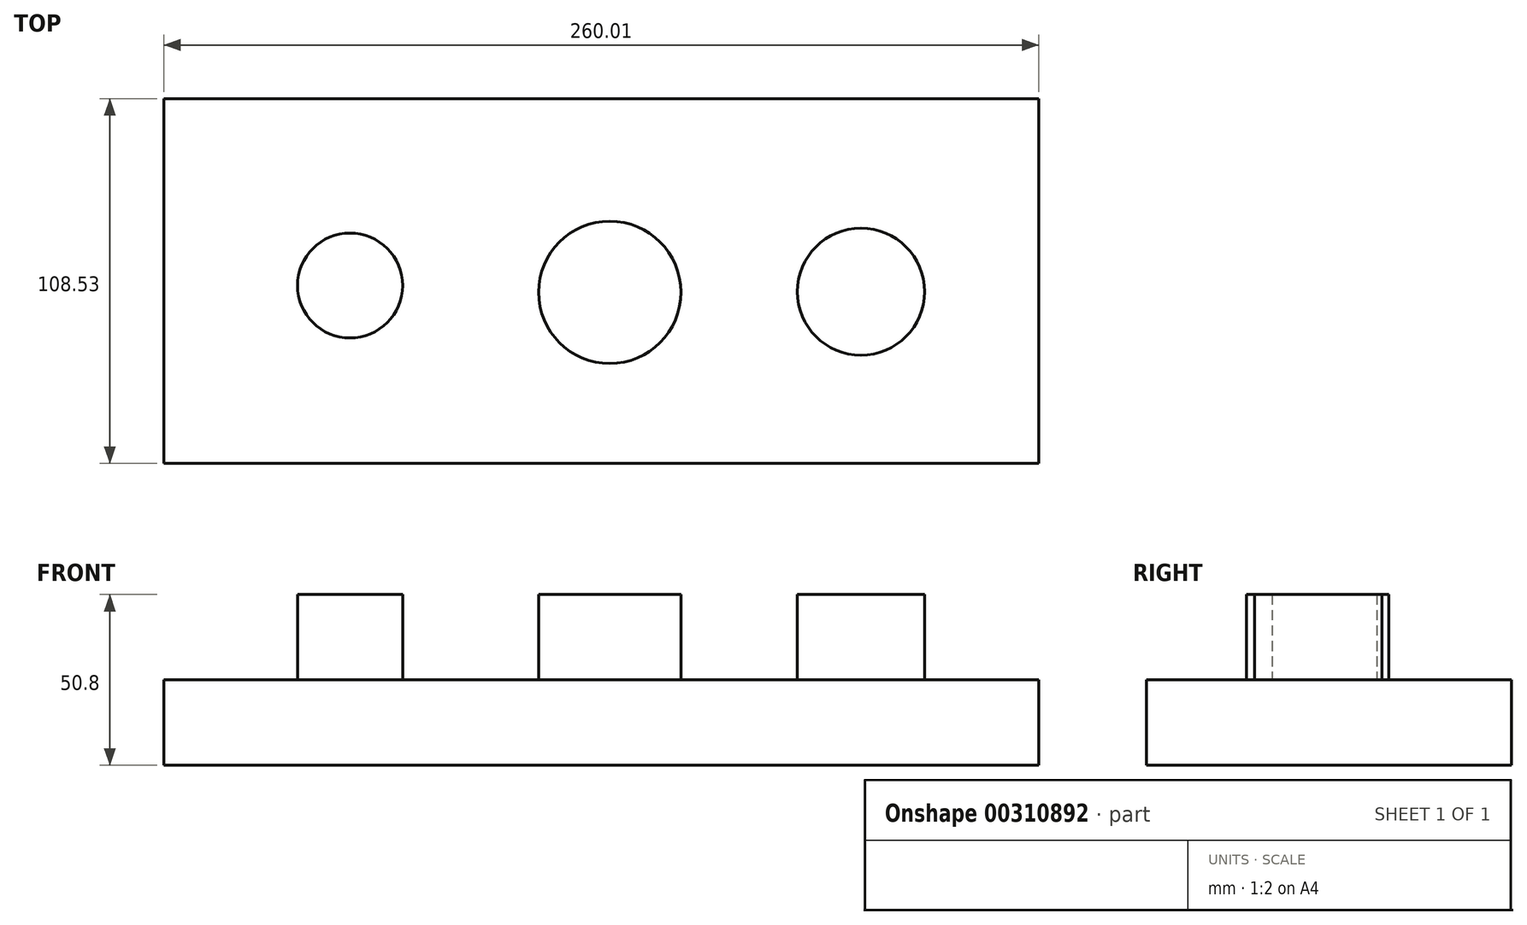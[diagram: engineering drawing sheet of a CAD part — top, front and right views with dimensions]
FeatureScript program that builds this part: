
annotation { "Feature Type Name" : "Feature", "Feature Type Description" : "" }
export const myFeature = defineFeature(function(context is Context, id is Id, definition is map)
    precondition{}
    {
        {
            var Q0;
            Q0=qCreatedBy(makeId("Top.planeOp"),FACE);
            var sketch = newSketch(context, id + "F0", { "sketchPlane" : qUnion([Q0])});
            skLineSegment(sketch, "E0.bottom", {"start": v(-124.02, 41.78) * mm, "end": v(135.99, 41.78) * mm});
            skLineSegment(sketch, "E0.top", {"start": v(-124.02, -66.75) * mm, "end": v(135.99, -66.75) * mm});
            skLineSegment(sketch, "E0.left", {"start": v(-124.02, 41.78) * mm, "end": v(-124.02, -66.75) * mm});
            skLineSegment(sketch, "E0.right", {"start": v(135.99, 41.78) * mm, "end": v(135.99, -66.75) * mm});
            skSolve(sketch);
        }
        {
            var Q0;
            Q0=makeQuery(id+"F0.imprint","IMPRINT",FACE,{"disambiguationData":[TD([[makeQuery(id+"F0.imprint","IMPRINT",EDGE,{"derivedFrom":sQuery(id+"F0.wireOp",EDGE,"E0.bottom")}),-1.0]])]});
            extrude(context, id + "F1", {"entities" : qUnion([Q0]), "depth" : 25.4 * mm});
        }
        {
            var Q0;
            Q0=makeQuery(id+"F1.opExtrude","CAP_FACE",FACE,{"disambiguationData":[OSD([sQuery(id+"F0.wireOp",EDGE,"E0.bottom"),sQuery(id+"F0.wireOp",EDGE,"E0.top"),sQuery(id+"F0.wireOp",EDGE,"E0.left"),sQuery(id+"F0.wireOp",EDGE,"E0.right")])],"isStart":false});
            var sketch = newSketch(context, id + "F2", { "sketchPlane" : qUnion([Q0])});
            skCircle(sketch, "E1", {"center": v(-68.63, -13.82) * mm, "radius": 15.61 * mm});
            skCircle(sketch, "E2", {"center": v(8.54, -15.85) * mm, "radius": 21.15 * mm});
            skCircle(sketch, "E3", {"center": v(83.2, -15.65) * mm, "radius": 18.9 * mm});
            skSolve(sketch);
        }
        {
            var Q0;
            Q0=qSketchRegion(id+"F2",true);
            extrude(context, id + "F3", {"entities" : qUnion([Q0]), "operationType" : NewBodyOperationType.ADD, "depth" : 25.4 * mm});
        }
    });
